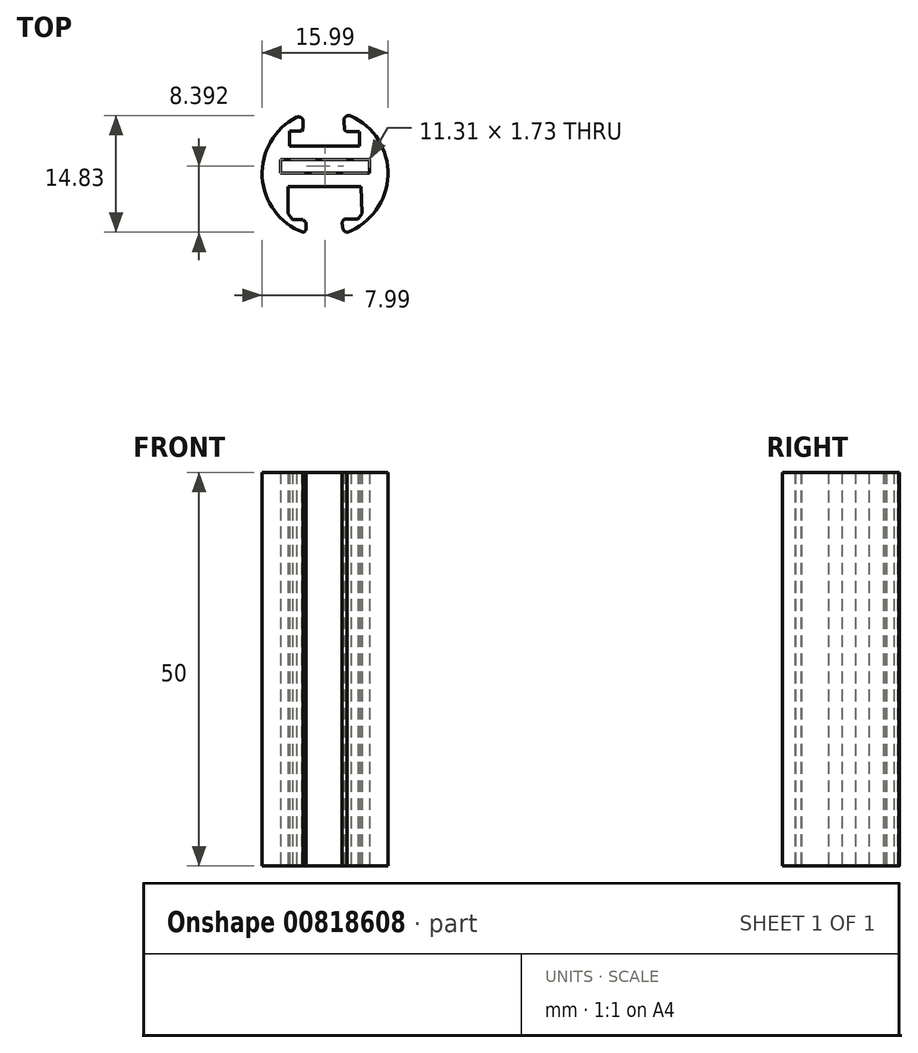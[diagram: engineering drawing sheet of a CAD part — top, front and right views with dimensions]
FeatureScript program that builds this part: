
annotation { "Feature Type Name" : "Feature", "Feature Type Description" : "" }
export const myFeature = defineFeature(function(context is Context, id is Id, definition is map)
    precondition{}
    {
        {
            var Q0;
            Q0=qCreatedBy(makeId("Top.planeOp"),FACE);
            var sketch = newSketch(context, id + "F0", { "sketchPlane" : qUnion([Q0])});
            skLineSegment(sketch, "E0", {"start": v(-4.52, 3.46) * mm, "end": v(4.4, 3.46) * mm});
            skLineSegment(sketch, "E1", {"start": v(4.4, 3.46) * mm, "end": v(4.4, 5.3) * mm});
            skLineSegment(sketch, "E2", {"start": v(4.4, 5.3) * mm, "end": v(2.72, 5.3) * mm});
            skLineSegment(sketch, "E3", {"start": v(-4.52, 3.46) * mm, "end": v(-4.52, 5.37) * mm});
            skLineSegment(sketch, "E4", {"start": v(-2.98, 5.37) * mm, "end": v(-2.77, 5.7) * mm});
            skLineSegment(sketch, "E5", {"start": v(-4.52, 5.37) * mm, "end": v(-2.98, 5.37) * mm});
            skLineSegment(sketch, "E6", {"start": v(-4.7, -1.67) * mm, "end": v(4.56, -1.67) * mm});
            skLineSegment(sketch, "E7", {"start": v(4.56, -1.67) * mm, "end": v(4.72, -5.13) * mm});
            skLineSegment(sketch, "E8", {"start": v(4.72, -5.13) * mm, "end": v(4.18, -5.83) * mm});
            skLineSegment(sketch, "E9", {"start": v(4.18, -5.83) * mm, "end": v(2.52, -5.83) * mm});
            skLineSegment(sketch, "E10", {"start": v(-4.7, -1.67) * mm, "end": v(-4.7, -5.1) * mm});
            skLineSegment(sketch, "E11", {"start": v(-4.7, -5.1) * mm, "end": v(-4.14, -5.9) * mm});
            skLineSegment(sketch, "E12", {"start": v(-4.14, -5.9) * mm, "end": v(-2.77, -5.9) * mm});
            skFitSpline(sketch, "E13", {"points": [v(-2.77, -5.9) * mm, v(-2.41, -6.35) * mm, v(-2.41, -6.63) * mm, v(-2.41, -7.01) * mm, v(-2.46, -7.24) * mm, v(-2.77, -7.5) * mm], "startDerivative": vector(1.9, -1.9) * mm, "endDerivative": vector(-1.84, -1.22) * mm});
            skFitSpline(sketch, "E14", {"points": [v(2.52, -5.83) * mm, v(2.22, -6.13) * mm, v(2.22, -6.7) * mm, v(2.32, -7.13) * mm, v(2.52, -7.4) * mm, v(2.8, -7.5) * mm], "startDerivative": vector(-1.8, -1.2) * mm, "endDerivative": vector(1.75, -0.3) * mm});
            skArc(sketch, "E15", {"start": v(-3.61, 7.13) * mm, "mid": v(-7.98, -0.46) * mm, "end": v(-2.77, -7.5) * mm});
            skArc(sketch, "E16", {"start": v(3.24, 7.31) * mm, "mid": v(8, -0.24) * mm, "end": v(2.8, -7.5) * mm});
            skArc(sketch, "E17", {"start": v(-3.61, 7.12) * mm, "mid": v(-3.07, 7.1) * mm, "end": v(-2.75, 6.65) * mm});
            skLineSegment(sketch, "E18", {"start": v(-2.75, 6.65) * mm, "end": v(-2.77, 5.7) * mm});
            skLineSegment(sketch, "E19", {"start": v(2.45, 5.52) * mm, "end": v(2.72, 5.3) * mm});
            skLineSegment(sketch, "E20", {"start": v(2.4, 6.68) * mm, "end": v(2.45, 5.52) * mm});
            skArc(sketch, "E21", {"start": v(3.28, 7.3) * mm, "mid": v(2.67, 7.23) * mm, "end": v(2.4, 6.68) * mm});
            skLineSegment(sketch, "E22.bottom", {"start": v(-5.65, 1.77) * mm, "end": v(5.65, 1.77) * mm});
            skLineSegment(sketch, "E22.top", {"start": v(-5.65, 0.04) * mm, "end": v(5.65, 0.04) * mm});
            skLineSegment(sketch, "E22.left", {"start": v(-5.65, 1.77) * mm, "end": v(-5.65, 0.04) * mm});
            skLineSegment(sketch, "E22.right", {"start": v(5.65, 1.77) * mm, "end": v(5.65, 0.04) * mm});
            skPoint(sketch, "E22.middle", {"position": v(0, 0.9) * mm});
            skSolve(sketch);
        }
        {
            var Q0;
            Q0=makeQuery(id+"F0.imprint","IMPRINT",FACE,{"disambiguationData":[TD([[makeQuery(id+"F0.imprint","IMPRINT",EDGE,{"derivedFrom":sQuery(id+"F0.wireOp",EDGE,"E0")}),-1.0]])]});
            extrude(context, id + "F1", {"entities" : qUnion([Q0]), "depth" : 50 * mm, "offsetDistance" : 25 * mm});
        }
    });
